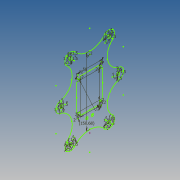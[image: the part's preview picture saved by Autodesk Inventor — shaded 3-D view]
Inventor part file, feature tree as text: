
AUTODESK INVENTOR PART (.ipt)
format: ipt  version: 2014 (Build 180170000, 170)  size: 141,824 bytes
history: native  units: mm
features: sketch x3
ambient origin geometry x8: Origin, YZ Plane, XZ Plane, XY Plane, X Axis, Y Axis, Z Axis, Center Point
feature tree (3):
  sketch  "Sketch1"  dims[d1=60.0mm]
  sketch  "Sketch2"  dims[d2=25.0mm]
  sketch  "Sketch3"  dims[d3=2.0mm d4=2.0mm d5=25.0mm d6=7.0mm d7=25.0mm d8=7.0mm d9=150.680282mm d10=25.0mm d11=7.0mm d12=1.5mm d13=1.5mm d14=1.5mm d15=1.5mm d16=2.0mm d17=1.5mm d18=1.5mm d19=1.5mm d20=1.5mm d21=1.5mm d22=1.5mm d23=1.5mm d24=1.5mm d25=1.5mm d26=1.5mm d27=1.5mm d28=1.5mm d29=1.5mm d30=1.5mm d31=1.5mm d32=1.5mm d33=25.0mm d34=25.0mm d35=7.0mm d36=7.0mm d37=1.5mm d38=1.5mm d39=1.5mm d40=1.5mm d41=2.0mm d42=2.0mm d43=2.0mm d44=2.0mm d45=2.0mm d46=8.0mm d47=2.0mm d48=8.0mm d49=2.0mm d50=8.0mm d51=42.0mm d52=60.0mm d53=42.0mm d54=58.0mm d55=60.0mm d56=42.0mm d57=7.0mm d59=8.5mm]
